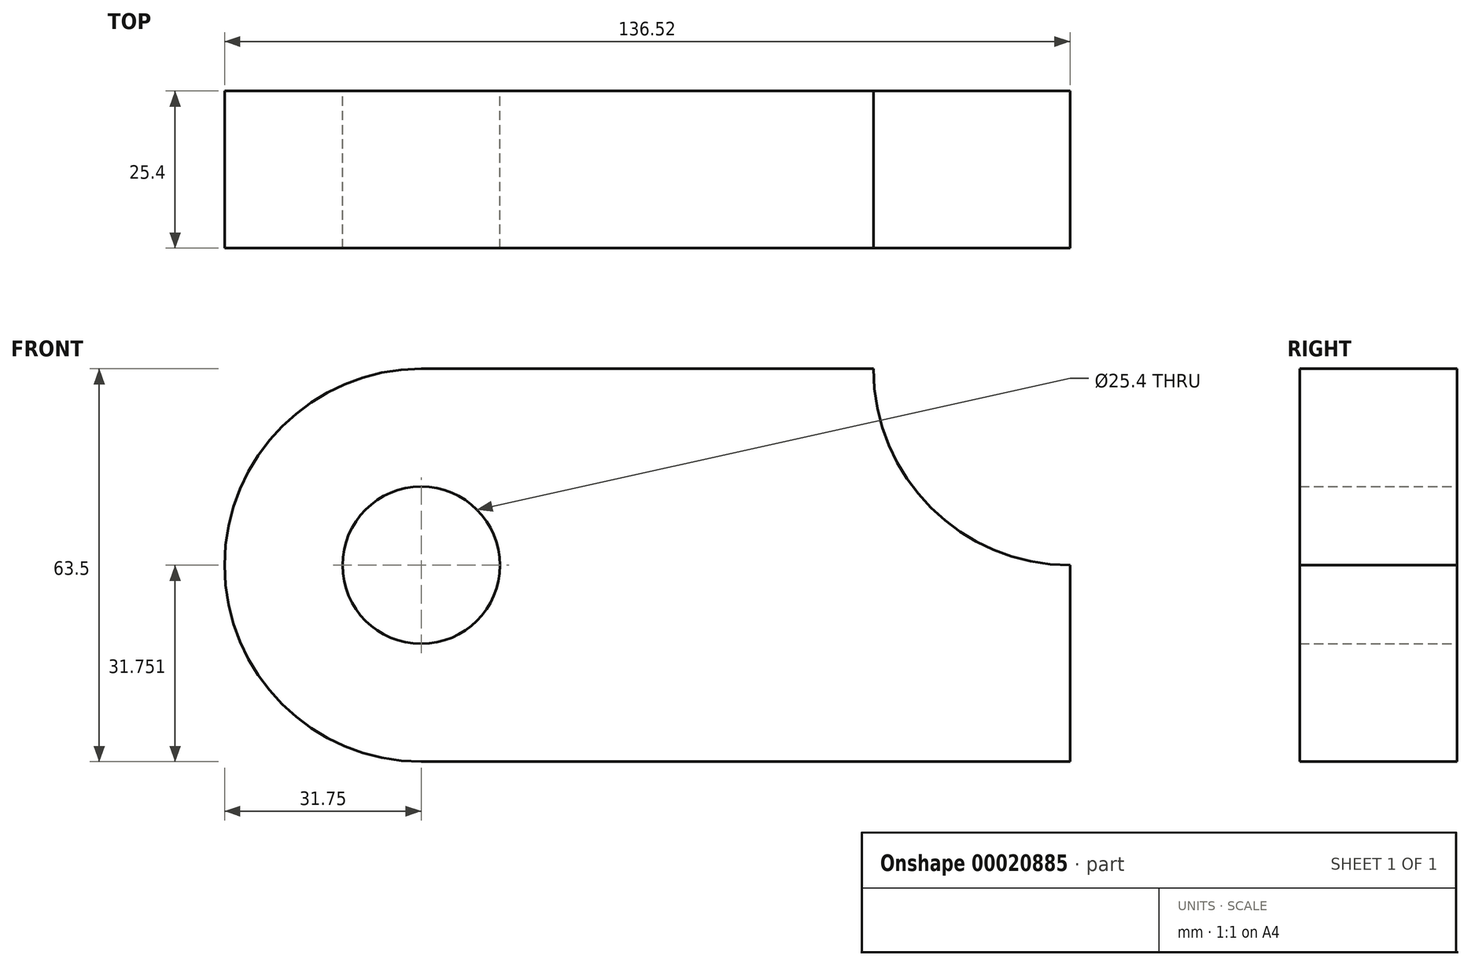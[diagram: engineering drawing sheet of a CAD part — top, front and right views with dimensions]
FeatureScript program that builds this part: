
annotation { "Feature Type Name" : "Feature", "Feature Type Description" : "" }
export const myFeature = defineFeature(function(context is Context, id is Id, definition is map)
    precondition{}
    {
        {
            var Q0;
            Q0=qCreatedBy(makeId("Front.planeOp"),FACE);
            var sketch = newSketch(context, id + "F0", { "sketchPlane" : qUnion([Q0])});
            skLineSegment(sketch, "E0.bottom", {"start": v(-56.16, 37.02) * mm, "end": v(16.86, 37.02) * mm});
            skLineSegment(sketch, "E0.top", {"start": v(-56.16, -26.48) * mm, "end": v(48.61, -26.48) * mm});
            skLineSegment(sketch, "E0.right", {"start": v(48.61, 5.27) * mm, "end": v(48.61, -26.48) * mm});
            skArc(sketch, "E1", {"start": v(-56.16, 37.02) * mm, "mid": v(-87.91, 5.27) * mm, "end": v(-56.16, -26.48) * mm});
            skArc(sketch, "E2", {"start": v(16.86, 37.02) * mm, "mid": v(26.16, 14.57) * mm, "end": v(48.61, 5.27) * mm});
            skCircle(sketch, "E3", {"center": v(-56.16, 5.27) * mm, "radius": 12.7 * mm});
            skSolve(sketch);
        }
        {
            var Q0;
            Q0 = qSketchRegion(id + "F0", true);
            extrude(context, id + "F1", {"entities" : qUnion([Q0]), "depth" : 25.4 * mm});
        }
    });
